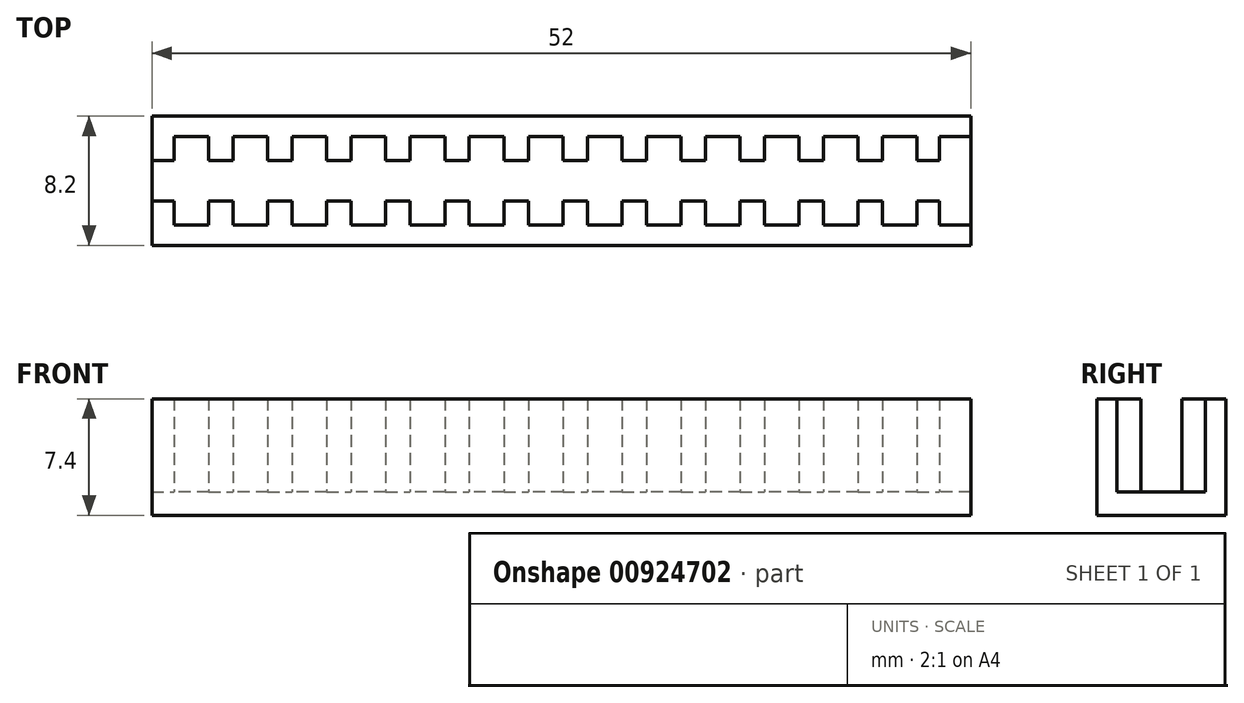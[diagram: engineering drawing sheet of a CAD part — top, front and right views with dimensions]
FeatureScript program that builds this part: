
annotation { "Feature Type Name" : "Feature", "Feature Type Description" : "" }
export const myFeature = defineFeature(function(context is Context, id is Id, definition is map)
    precondition{}
    {
        {
            assignVariable(context, id + "F0", {"name" : "Thickness", "anyValue" : 1.5});
        }
        {
            var Q0;
            Q0=qCreatedBy(makeId("Top.planeOp"),FACE);
            var sketch = newSketch(context, id + "F1", { "sketchPlane" : qUnion([Q0])});
            skLineSegment(sketch, "E0.bottom", {"start": v(0, 0) * mm, "end": v(52, 0) * mm});
            skLineSegment(sketch, "E0.top", {"start": v(0, -8.2) * mm, "end": v(52, -8.2) * mm});
            skLineSegment(sketch, "E0.left", {"start": v(0, 0) * mm, "end": v(0, -8.2) * mm});
            skLineSegment(sketch, "E0.right", {"start": v(52, 0) * mm, "end": v(52, -8.2) * mm});
            skLineSegment(sketch, "E1.top", {"start": v(0, -1.3) * mm, "end": v(52, -1.3) * mm});
            skLineSegment(sketch, "E1.left", {"start": v(0, 0) * mm, "end": v(0, -1.3) * mm});
            skLineSegment(sketch, "E1.right", {"start": v(52, 0) * mm, "end": v(52, -1.3) * mm});
            skLineSegment(sketch, "E2.bottom", {"start": v(0, -6.9) * mm, "end": v(52, -6.9) * mm});
            skLineSegment(sketch, "E2.left", {"start": v(0, -6.9) * mm, "end": v(0, -8.2) * mm});
            skLineSegment(sketch, "E2.right", {"start": v(52, -6.9) * mm, "end": v(52, -8.2) * mm});
            skLineSegment(sketch, "E3", {"start": v(2, -1.3) * mm, "end": v(2, 0) * mm, "construction": true});
            skLineSegment(sketch, "E4", {"start": v(2.26, -6.9) * mm, "end": v(2.26, -8.2) * mm, "construction": true});
            skSolve(sketch);
        }
        {
            var Q0;
            Q0 = qSketchRegion(id + "F1", true);
            extrude(context, id + "F2", {"entities" : qUnion([Q0]), "depth" : (getVariable(context, 'Thickness')) * mm, "offsetDistance" : 25 * mm});
        }
        {
            var Q0;
            Q0=makeQuery(id+"F1.imprint","IMPRINT",FACE,{"disambiguationData":[TD([[makeQuery(id+"F1.imprint","IMPRINT",EDGE,{"derivedFrom":sQuery(id+"F1.wireOp",EDGE,"E2.bottom")}),-1.0]])]});
            var Q1;
            Q1=makeQuery(id+"F1.imprint","IMPRINT",FACE,{"disambiguationData":[TD([[makeQuery(id+"F1.imprint","IMPRINT",EDGE,{"derivedFrom":sQuery(id+"F1.wireOp",EDGE,"E0.bottom")}),-1.0]])]});
            extrude(context, id + "F3", {"entities" : qUnion([Q0, Q1]), "operationType" : NewBodyOperationType.ADD, "depth" : (4.4 + getVariable(context, 'Thickness') * 2) * mm, "offsetDistance" : 25 * mm});
        }
        {
            var Q0;
            Q0=makeQuery(id+"F2.opExtrude","CAP_FACE",FACE,{"disambiguationData":[OSD([sQuery(id+"F1.wireOp",EDGE,"E0.left"),sQuery(id+"F1.wireOp",EDGE,"E0.right"),sQuery(id+"F1.wireOp",EDGE,"E0.bottom"),sQuery(id+"F1.wireOp",EDGE,"E1.left"),sQuery(id+"F1.wireOp",EDGE,"E1.right"),sQuery(id+"F1.wireOp",EDGE,"E0.top"),sQuery(id+"F1.wireOp",EDGE,"E2.left"),sQuery(id+"F1.wireOp",EDGE,"E2.right")])],"isStart":false});
            var sketch = newSketch(context, id + "F4", { "sketchPlane" : qUnion([Q0])});
            skLineSegment(sketch, "E5.bottom", {"start": v(0, -1.3) * mm, "end": v(1.4, -1.3) * mm});
            skLineSegment(sketch, "E5.top", {"start": v(0, -2.8) * mm, "end": v(1.4, -2.8) * mm});
            skLineSegment(sketch, "E5.left", {"start": v(0, -1.3) * mm, "end": v(0, -2.8) * mm});
            skLineSegment(sketch, "E5.right", {"start": v(1.4, -1.3) * mm, "end": v(1.4, -2.8) * mm});
            skLineSegment(sketch, "E6.bottom", {"start": v(0, -6.9) * mm, "end": v(1.4, -6.9) * mm});
            skLineSegment(sketch, "E6.top", {"start": v(0, -5.4) * mm, "end": v(1.4, -5.4) * mm});
            skLineSegment(sketch, "E6.left", {"start": v(0, -6.9) * mm, "end": v(0, -5.4) * mm});
            skLineSegment(sketch, "E6.right", {"start": v(1.4, -6.9) * mm, "end": v(1.4, -5.4) * mm});
            skLineSegment(sketch, "E7.bottom", {"start": v(3.6, -2.8) * mm, "end": v(5, -2.8) * mm});
            skLineSegment(sketch, "E7.top", {"start": v(3.6, -1.3) * mm, "end": v(5, -1.3) * mm});
            skLineSegment(sketch, "E7.left", {"start": v(3.6, -2.8) * mm, "end": v(3.6, -1.3) * mm});
            skLineSegment(sketch, "E7.right", {"start": v(5, -2.8) * mm, "end": v(5, -1.3) * mm});
            skLineSegment(sketch, "E8.bottom", {"start": v(3.6, -5.4) * mm, "end": v(5, -5.4) * mm});
            skLineSegment(sketch, "E8.top", {"start": v(3.6, -6.9) * mm, "end": v(5, -6.9) * mm});
            skLineSegment(sketch, "E8.left", {"start": v(3.6, -5.4) * mm, "end": v(3.6, -6.9) * mm});
            skLineSegment(sketch, "E8.right", {"start": v(5, -5.4) * mm, "end": v(5, -6.9) * mm});
            skLineSegment(sketch, "E9.1.0.0", {"start": v(3.75, -2.8) * mm, "end": v(5.15, -2.8) * mm});
            skLineSegment(sketch, "E9.1.0.1", {"start": v(5.15, -1.3) * mm, "end": v(5.15, -2.8) * mm});
            skLineSegment(sketch, "E9.1.0.2", {"start": v(3.75, -6.9) * mm, "end": v(5.15, -6.9) * mm});
            skLineSegment(sketch, "E9.1.0.3", {"start": v(3.75, -6.9) * mm, "end": v(3.75, -5.4) * mm});
            skLineSegment(sketch, "E9.1.0.4", {"start": v(7.35, -1.3) * mm, "end": v(8.75, -1.3) * mm});
            skLineSegment(sketch, "E9.1.0.5", {"start": v(3.75, -1.3) * mm, "end": v(5.15, -1.3) * mm});
            skLineSegment(sketch, "E9.1.0.6", {"start": v(7.35, -5.4) * mm, "end": v(8.75, -5.4) * mm});
            skLineSegment(sketch, "E9.1.0.7", {"start": v(7.35, -2.8) * mm, "end": v(7.35, -1.3) * mm});
            skLineSegment(sketch, "E9.1.0.8", {"start": v(5.15, -6.9) * mm, "end": v(5.15, -5.4) * mm});
            skLineSegment(sketch, "E9.1.0.9", {"start": v(7.35, -6.9) * mm, "end": v(8.75, -6.9) * mm});
            skLineSegment(sketch, "E9.1.0.10", {"start": v(8.75, -5.4) * mm, "end": v(8.75, -6.9) * mm});
            skLineSegment(sketch, "E9.1.0.11", {"start": v(3.75, -1.3) * mm, "end": v(3.75, -2.8) * mm});
            skLineSegment(sketch, "E9.1.0.12", {"start": v(7.35, -2.8) * mm, "end": v(8.75, -2.8) * mm});
            skLineSegment(sketch, "E9.1.0.13", {"start": v(7.35, -5.4) * mm, "end": v(7.35, -6.9) * mm});
            skLineSegment(sketch, "E9.1.0.14", {"start": v(3.75, -5.4) * mm, "end": v(5.15, -5.4) * mm});
            skLineSegment(sketch, "E9.1.0.15", {"start": v(8.75, -2.8) * mm, "end": v(8.75, -1.3) * mm});
            skLineSegment(sketch, "E9.2.0.0", {"start": v(7.5, -2.8) * mm, "end": v(8.9, -2.8) * mm});
            skLineSegment(sketch, "E9.2.0.1", {"start": v(8.9, -1.3) * mm, "end": v(8.9, -2.8) * mm});
            skLineSegment(sketch, "E9.2.0.2", {"start": v(7.5, -6.9) * mm, "end": v(8.9, -6.9) * mm});
            skLineSegment(sketch, "E9.2.0.3", {"start": v(7.5, -6.9) * mm, "end": v(7.5, -5.4) * mm});
            skLineSegment(sketch, "E9.2.0.4", {"start": v(11.1, -1.3) * mm, "end": v(12.5, -1.3) * mm});
            skLineSegment(sketch, "E9.2.0.5", {"start": v(7.5, -1.3) * mm, "end": v(8.9, -1.3) * mm});
            skLineSegment(sketch, "E9.2.0.6", {"start": v(11.1, -5.4) * mm, "end": v(12.5, -5.4) * mm});
            skLineSegment(sketch, "E9.2.0.7", {"start": v(11.1, -2.8) * mm, "end": v(11.1, -1.3) * mm});
            skLineSegment(sketch, "E9.2.0.8", {"start": v(8.9, -6.9) * mm, "end": v(8.9, -5.4) * mm});
            skLineSegment(sketch, "E9.2.0.9", {"start": v(11.1, -6.9) * mm, "end": v(12.5, -6.9) * mm});
            skLineSegment(sketch, "E9.2.0.10", {"start": v(12.5, -5.4) * mm, "end": v(12.5, -6.9) * mm});
            skLineSegment(sketch, "E9.2.0.11", {"start": v(7.5, -1.3) * mm, "end": v(7.5, -2.8) * mm});
            skLineSegment(sketch, "E9.2.0.12", {"start": v(11.1, -2.8) * mm, "end": v(12.5, -2.8) * mm});
            skLineSegment(sketch, "E9.2.0.13", {"start": v(11.1, -5.4) * mm, "end": v(11.1, -6.9) * mm});
            skLineSegment(sketch, "E9.2.0.14", {"start": v(7.5, -5.4) * mm, "end": v(8.9, -5.4) * mm});
            skLineSegment(sketch, "E9.2.0.15", {"start": v(12.5, -2.8) * mm, "end": v(12.5, -1.3) * mm});
            skLineSegment(sketch, "E9.direction1", {"start": v(0, -6.9) * mm, "end": v(3.75, -6.9) * mm, "construction": true});
            skLineSegment(sketch, "E10.0.3.0", {"start": v(11.25, -2.8) * mm, "end": v(12.65, -2.8) * mm});
            skLineSegment(sketch, "E10.3.3.0", {"start": v(12.65, -1.3) * mm, "end": v(12.65, -2.8) * mm});
            skLineSegment(sketch, "E10.6.3.0", {"start": v(11.25, -6.9) * mm, "end": v(12.65, -6.9) * mm});
            skLineSegment(sketch, "E10.9.3.0", {"start": v(11.25, -6.9) * mm, "end": v(11.25, -5.4) * mm});
            skLineSegment(sketch, "E10.12.3.0", {"start": v(14.85, -1.3) * mm, "end": v(16.25, -1.3) * mm});
            skLineSegment(sketch, "E10.15.3.0", {"start": v(11.25, -1.3) * mm, "end": v(12.65, -1.3) * mm});
            skLineSegment(sketch, "E10.18.3.0", {"start": v(14.85, -5.4) * mm, "end": v(16.25, -5.4) * mm});
            skLineSegment(sketch, "E10.21.3.0", {"start": v(14.85, -2.8) * mm, "end": v(14.85, -1.3) * mm});
            skLineSegment(sketch, "E10.24.3.0", {"start": v(12.65, -6.9) * mm, "end": v(12.65, -5.4) * mm});
            skLineSegment(sketch, "E10.27.3.0", {"start": v(14.85, -6.9) * mm, "end": v(16.25, -6.9) * mm});
            skLineSegment(sketch, "E10.30.3.0", {"start": v(16.25, -5.4) * mm, "end": v(16.25, -6.9) * mm});
            skLineSegment(sketch, "E10.33.3.0", {"start": v(11.25, -1.3) * mm, "end": v(11.25, -2.8) * mm});
            skLineSegment(sketch, "E10.36.3.0", {"start": v(14.85, -2.8) * mm, "end": v(16.25, -2.8) * mm});
            skLineSegment(sketch, "E10.39.3.0", {"start": v(14.85, -5.4) * mm, "end": v(14.85, -6.9) * mm});
            skLineSegment(sketch, "E10.42.3.0", {"start": v(11.25, -5.4) * mm, "end": v(12.65, -5.4) * mm});
            skLineSegment(sketch, "E10.45.3.0", {"start": v(16.25, -2.8) * mm, "end": v(16.25, -1.3) * mm});
            skLineSegment(sketch, "E10.0.4.0", {"start": v(15, -2.8) * mm, "end": v(16.4, -2.8) * mm});
            skLineSegment(sketch, "E10.3.4.0", {"start": v(16.4, -1.3) * mm, "end": v(16.4, -2.8) * mm});
            skLineSegment(sketch, "E10.6.4.0", {"start": v(15, -6.9) * mm, "end": v(16.4, -6.9) * mm});
            skLineSegment(sketch, "E10.9.4.0", {"start": v(15, -6.9) * mm, "end": v(15, -5.4) * mm});
            skLineSegment(sketch, "E10.12.4.0", {"start": v(18.6, -1.3) * mm, "end": v(20, -1.3) * mm});
            skLineSegment(sketch, "E10.15.4.0", {"start": v(15, -1.3) * mm, "end": v(16.4, -1.3) * mm});
            skLineSegment(sketch, "E10.18.4.0", {"start": v(18.6, -5.4) * mm, "end": v(20, -5.4) * mm});
            skLineSegment(sketch, "E10.21.4.0", {"start": v(18.6, -2.8) * mm, "end": v(18.6, -1.3) * mm});
            skLineSegment(sketch, "E10.24.4.0", {"start": v(16.4, -6.9) * mm, "end": v(16.4, -5.4) * mm});
            skLineSegment(sketch, "E10.27.4.0", {"start": v(18.6, -6.9) * mm, "end": v(20, -6.9) * mm});
            skLineSegment(sketch, "E10.30.4.0", {"start": v(20, -5.4) * mm, "end": v(20, -6.9) * mm});
            skLineSegment(sketch, "E10.33.4.0", {"start": v(15, -1.3) * mm, "end": v(15, -2.8) * mm});
            skLineSegment(sketch, "E10.36.4.0", {"start": v(18.6, -2.8) * mm, "end": v(20, -2.8) * mm});
            skLineSegment(sketch, "E10.39.4.0", {"start": v(18.6, -5.4) * mm, "end": v(18.6, -6.9) * mm});
            skLineSegment(sketch, "E10.42.4.0", {"start": v(15, -5.4) * mm, "end": v(16.4, -5.4) * mm});
            skLineSegment(sketch, "E10.45.4.0", {"start": v(20, -2.8) * mm, "end": v(20, -1.3) * mm});
            skLineSegment(sketch, "E10.0.5.0", {"start": v(18.75, -2.8) * mm, "end": v(20.15, -2.8) * mm});
            skLineSegment(sketch, "E10.3.5.0", {"start": v(20.15, -1.3) * mm, "end": v(20.15, -2.8) * mm});
            skLineSegment(sketch, "E10.6.5.0", {"start": v(18.75, -6.9) * mm, "end": v(20.15, -6.9) * mm});
            skLineSegment(sketch, "E10.9.5.0", {"start": v(18.75, -6.9) * mm, "end": v(18.75, -5.4) * mm});
            skLineSegment(sketch, "E10.12.5.0", {"start": v(22.35, -1.3) * mm, "end": v(23.75, -1.3) * mm});
            skLineSegment(sketch, "E10.15.5.0", {"start": v(18.75, -1.3) * mm, "end": v(20.15, -1.3) * mm});
            skLineSegment(sketch, "E10.18.5.0", {"start": v(22.35, -5.4) * mm, "end": v(23.75, -5.4) * mm});
            skLineSegment(sketch, "E10.21.5.0", {"start": v(22.35, -2.8) * mm, "end": v(22.35, -1.3) * mm});
            skLineSegment(sketch, "E10.24.5.0", {"start": v(20.15, -6.9) * mm, "end": v(20.15, -5.4) * mm});
            skLineSegment(sketch, "E10.27.5.0", {"start": v(22.35, -6.9) * mm, "end": v(23.75, -6.9) * mm});
            skLineSegment(sketch, "E10.30.5.0", {"start": v(23.75, -5.4) * mm, "end": v(23.75, -6.9) * mm});
            skLineSegment(sketch, "E10.33.5.0", {"start": v(18.75, -1.3) * mm, "end": v(18.75, -2.8) * mm});
            skLineSegment(sketch, "E10.36.5.0", {"start": v(22.35, -2.8) * mm, "end": v(23.75, -2.8) * mm});
            skLineSegment(sketch, "E10.39.5.0", {"start": v(22.35, -5.4) * mm, "end": v(22.35, -6.9) * mm});
            skLineSegment(sketch, "E10.42.5.0", {"start": v(18.75, -5.4) * mm, "end": v(20.15, -5.4) * mm});
            skLineSegment(sketch, "E10.45.5.0", {"start": v(23.75, -2.8) * mm, "end": v(23.75, -1.3) * mm});
            skLineSegment(sketch, "E10.0.6.0", {"start": v(22.5, -2.8) * mm, "end": v(23.9, -2.8) * mm});
            skLineSegment(sketch, "E10.3.6.0", {"start": v(23.9, -1.3) * mm, "end": v(23.9, -2.8) * mm});
            skLineSegment(sketch, "E10.6.6.0", {"start": v(22.5, -6.9) * mm, "end": v(23.9, -6.9) * mm});
            skLineSegment(sketch, "E10.9.6.0", {"start": v(22.5, -6.9) * mm, "end": v(22.5, -5.4) * mm});
            skLineSegment(sketch, "E10.12.6.0", {"start": v(26.1, -1.3) * mm, "end": v(27.5, -1.3) * mm});
            skLineSegment(sketch, "E10.15.6.0", {"start": v(22.5, -1.3) * mm, "end": v(23.9, -1.3) * mm});
            skLineSegment(sketch, "E10.18.6.0", {"start": v(26.1, -5.4) * mm, "end": v(27.5, -5.4) * mm});
            skLineSegment(sketch, "E10.21.6.0", {"start": v(26.1, -2.8) * mm, "end": v(26.1, -1.3) * mm});
            skLineSegment(sketch, "E10.24.6.0", {"start": v(23.9, -6.9) * mm, "end": v(23.9, -5.4) * mm});
            skLineSegment(sketch, "E10.27.6.0", {"start": v(26.1, -6.9) * mm, "end": v(27.5, -6.9) * mm});
            skLineSegment(sketch, "E10.30.6.0", {"start": v(27.5, -5.4) * mm, "end": v(27.5, -6.9) * mm});
            skLineSegment(sketch, "E10.33.6.0", {"start": v(22.5, -1.3) * mm, "end": v(22.5, -2.8) * mm});
            skLineSegment(sketch, "E10.36.6.0", {"start": v(26.1, -2.8) * mm, "end": v(27.5, -2.8) * mm});
            skLineSegment(sketch, "E10.39.6.0", {"start": v(26.1, -5.4) * mm, "end": v(26.1, -6.9) * mm});
            skLineSegment(sketch, "E10.42.6.0", {"start": v(22.5, -5.4) * mm, "end": v(23.9, -5.4) * mm});
            skLineSegment(sketch, "E10.45.6.0", {"start": v(27.5, -2.8) * mm, "end": v(27.5, -1.3) * mm});
            skLineSegment(sketch, "E10.0.7.0", {"start": v(26.25, -2.8) * mm, "end": v(27.65, -2.8) * mm});
            skLineSegment(sketch, "E10.3.7.0", {"start": v(27.65, -1.3) * mm, "end": v(27.65, -2.8) * mm});
            skLineSegment(sketch, "E10.6.7.0", {"start": v(26.25, -6.9) * mm, "end": v(27.65, -6.9) * mm});
            skLineSegment(sketch, "E10.9.7.0", {"start": v(26.25, -6.9) * mm, "end": v(26.25, -5.4) * mm});
            skLineSegment(sketch, "E10.12.7.0", {"start": v(29.85, -1.3) * mm, "end": v(31.25, -1.3) * mm});
            skLineSegment(sketch, "E10.15.7.0", {"start": v(26.25, -1.3) * mm, "end": v(27.65, -1.3) * mm});
            skLineSegment(sketch, "E10.18.7.0", {"start": v(29.85, -5.4) * mm, "end": v(31.25, -5.4) * mm});
            skLineSegment(sketch, "E10.21.7.0", {"start": v(29.85, -2.8) * mm, "end": v(29.85, -1.3) * mm});
            skLineSegment(sketch, "E10.24.7.0", {"start": v(27.65, -6.9) * mm, "end": v(27.65, -5.4) * mm});
            skLineSegment(sketch, "E10.27.7.0", {"start": v(29.85, -6.9) * mm, "end": v(31.25, -6.9) * mm});
            skLineSegment(sketch, "E10.30.7.0", {"start": v(31.25, -5.4) * mm, "end": v(31.25, -6.9) * mm});
            skLineSegment(sketch, "E10.33.7.0", {"start": v(26.25, -1.3) * mm, "end": v(26.25, -2.8) * mm});
            skLineSegment(sketch, "E10.36.7.0", {"start": v(29.85, -2.8) * mm, "end": v(31.25, -2.8) * mm});
            skLineSegment(sketch, "E10.39.7.0", {"start": v(29.85, -5.4) * mm, "end": v(29.85, -6.9) * mm});
            skLineSegment(sketch, "E10.42.7.0", {"start": v(26.25, -5.4) * mm, "end": v(27.65, -5.4) * mm});
            skLineSegment(sketch, "E10.45.7.0", {"start": v(31.25, -2.8) * mm, "end": v(31.25, -1.3) * mm});
            skLineSegment(sketch, "E11.0.8.0", {"start": v(30, -2.8) * mm, "end": v(31.4, -2.8) * mm});
            skLineSegment(sketch, "E11.3.8.0", {"start": v(31.4, -1.3) * mm, "end": v(31.4, -2.8) * mm});
            skLineSegment(sketch, "E11.6.8.0", {"start": v(30, -6.9) * mm, "end": v(31.4, -6.9) * mm});
            skLineSegment(sketch, "E11.9.8.0", {"start": v(30, -6.9) * mm, "end": v(30, -5.4) * mm});
            skLineSegment(sketch, "E11.12.8.0", {"start": v(33.6, -1.3) * mm, "end": v(35, -1.3) * mm});
            skLineSegment(sketch, "E11.15.8.0", {"start": v(30, -1.3) * mm, "end": v(31.4, -1.3) * mm});
            skLineSegment(sketch, "E11.18.8.0", {"start": v(33.6, -5.4) * mm, "end": v(35, -5.4) * mm});
            skLineSegment(sketch, "E11.21.8.0", {"start": v(33.6, -2.8) * mm, "end": v(33.6, -1.3) * mm});
            skLineSegment(sketch, "E11.24.8.0", {"start": v(31.4, -6.9) * mm, "end": v(31.4, -5.4) * mm});
            skLineSegment(sketch, "E11.27.8.0", {"start": v(33.6, -6.9) * mm, "end": v(35, -6.9) * mm});
            skLineSegment(sketch, "E11.30.8.0", {"start": v(35, -5.4) * mm, "end": v(35, -6.9) * mm});
            skLineSegment(sketch, "E11.33.8.0", {"start": v(30, -1.3) * mm, "end": v(30, -2.8) * mm});
            skLineSegment(sketch, "E11.36.8.0", {"start": v(33.6, -2.8) * mm, "end": v(35, -2.8) * mm});
            skLineSegment(sketch, "E11.39.8.0", {"start": v(33.6, -5.4) * mm, "end": v(33.6, -6.9) * mm});
            skLineSegment(sketch, "E11.42.8.0", {"start": v(30, -5.4) * mm, "end": v(31.4, -5.4) * mm});
            skLineSegment(sketch, "E11.45.8.0", {"start": v(35, -2.8) * mm, "end": v(35, -1.3) * mm});
            skLineSegment(sketch, "E12.0.9.0", {"start": v(33.75, -2.8) * mm, "end": v(35.15, -2.8) * mm});
            skLineSegment(sketch, "E12.3.9.0", {"start": v(35.15, -1.3) * mm, "end": v(35.15, -2.8) * mm});
            skLineSegment(sketch, "E12.6.9.0", {"start": v(33.75, -6.9) * mm, "end": v(35.15, -6.9) * mm});
            skLineSegment(sketch, "E12.9.9.0", {"start": v(33.75, -6.9) * mm, "end": v(33.75, -5.4) * mm});
            skLineSegment(sketch, "E12.12.9.0", {"start": v(37.35, -1.3) * mm, "end": v(38.75, -1.3) * mm});
            skLineSegment(sketch, "E12.15.9.0", {"start": v(33.75, -1.3) * mm, "end": v(35.15, -1.3) * mm});
            skLineSegment(sketch, "E12.18.9.0", {"start": v(37.35, -5.4) * mm, "end": v(38.75, -5.4) * mm});
            skLineSegment(sketch, "E12.21.9.0", {"start": v(37.35, -2.8) * mm, "end": v(37.35, -1.3) * mm});
            skLineSegment(sketch, "E12.24.9.0", {"start": v(35.15, -6.9) * mm, "end": v(35.15, -5.4) * mm});
            skLineSegment(sketch, "E12.27.9.0", {"start": v(37.35, -6.9) * mm, "end": v(38.75, -6.9) * mm});
            skLineSegment(sketch, "E12.30.9.0", {"start": v(38.75, -5.4) * mm, "end": v(38.75, -6.9) * mm});
            skLineSegment(sketch, "E12.33.9.0", {"start": v(33.75, -1.3) * mm, "end": v(33.75, -2.8) * mm});
            skLineSegment(sketch, "E12.36.9.0", {"start": v(37.35, -2.8) * mm, "end": v(38.75, -2.8) * mm});
            skLineSegment(sketch, "E12.39.9.0", {"start": v(37.35, -5.4) * mm, "end": v(37.35, -6.9) * mm});
            skLineSegment(sketch, "E12.42.9.0", {"start": v(33.75, -5.4) * mm, "end": v(35.15, -5.4) * mm});
            skLineSegment(sketch, "E12.45.9.0", {"start": v(38.75, -2.8) * mm, "end": v(38.75, -1.3) * mm});
            skLineSegment(sketch, "E13.0.10.0", {"start": v(37.5, -2.8) * mm, "end": v(38.9, -2.8) * mm});
            skLineSegment(sketch, "E13.3.10.0", {"start": v(38.9, -1.3) * mm, "end": v(38.9, -2.8) * mm});
            skLineSegment(sketch, "E13.6.10.0", {"start": v(37.5, -6.9) * mm, "end": v(38.9, -6.9) * mm});
            skLineSegment(sketch, "E13.9.10.0", {"start": v(37.5, -6.9) * mm, "end": v(37.5, -5.4) * mm});
            skLineSegment(sketch, "E13.12.10.0", {"start": v(41.1, -1.3) * mm, "end": v(42.5, -1.3) * mm});
            skLineSegment(sketch, "E13.15.10.0", {"start": v(37.5, -1.3) * mm, "end": v(38.9, -1.3) * mm});
            skLineSegment(sketch, "E13.18.10.0", {"start": v(41.1, -5.4) * mm, "end": v(42.5, -5.4) * mm});
            skLineSegment(sketch, "E13.21.10.0", {"start": v(41.1, -2.8) * mm, "end": v(41.1, -1.3) * mm});
            skLineSegment(sketch, "E13.24.10.0", {"start": v(38.9, -6.9) * mm, "end": v(38.9, -5.4) * mm});
            skLineSegment(sketch, "E13.27.10.0", {"start": v(41.1, -6.9) * mm, "end": v(42.5, -6.9) * mm});
            skLineSegment(sketch, "E13.30.10.0", {"start": v(42.5, -5.4) * mm, "end": v(42.5, -6.9) * mm});
            skLineSegment(sketch, "E13.33.10.0", {"start": v(37.5, -1.3) * mm, "end": v(37.5, -2.8) * mm});
            skLineSegment(sketch, "E13.36.10.0", {"start": v(41.1, -2.8) * mm, "end": v(42.5, -2.8) * mm});
            skLineSegment(sketch, "E13.39.10.0", {"start": v(41.1, -5.4) * mm, "end": v(41.1, -6.9) * mm});
            skLineSegment(sketch, "E13.42.10.0", {"start": v(37.5, -5.4) * mm, "end": v(38.9, -5.4) * mm});
            skLineSegment(sketch, "E13.45.10.0", {"start": v(42.5, -2.8) * mm, "end": v(42.5, -1.3) * mm});
            skLineSegment(sketch, "E13.0.11.0", {"start": v(41.25, -2.8) * mm, "end": v(42.65, -2.8) * mm});
            skLineSegment(sketch, "E13.3.11.0", {"start": v(42.65, -1.3) * mm, "end": v(42.65, -2.8) * mm});
            skLineSegment(sketch, "E13.6.11.0", {"start": v(41.25, -6.9) * mm, "end": v(42.65, -6.9) * mm});
            skLineSegment(sketch, "E13.9.11.0", {"start": v(41.25, -6.9) * mm, "end": v(41.25, -5.4) * mm});
            skLineSegment(sketch, "E13.12.11.0", {"start": v(44.85, -1.3) * mm, "end": v(46.25, -1.3) * mm});
            skLineSegment(sketch, "E13.15.11.0", {"start": v(41.25, -1.3) * mm, "end": v(42.65, -1.3) * mm});
            skLineSegment(sketch, "E13.18.11.0", {"start": v(44.85, -5.4) * mm, "end": v(46.25, -5.4) * mm});
            skLineSegment(sketch, "E13.21.11.0", {"start": v(44.85, -2.8) * mm, "end": v(44.85, -1.3) * mm});
            skLineSegment(sketch, "E13.24.11.0", {"start": v(42.65, -6.9) * mm, "end": v(42.65, -5.4) * mm});
            skLineSegment(sketch, "E13.27.11.0", {"start": v(44.85, -6.9) * mm, "end": v(46.25, -6.9) * mm});
            skLineSegment(sketch, "E13.30.11.0", {"start": v(46.25, -5.4) * mm, "end": v(46.25, -6.9) * mm});
            skLineSegment(sketch, "E13.33.11.0", {"start": v(41.25, -1.3) * mm, "end": v(41.25, -2.8) * mm});
            skLineSegment(sketch, "E13.36.11.0", {"start": v(44.85, -2.8) * mm, "end": v(46.25, -2.8) * mm});
            skLineSegment(sketch, "E13.39.11.0", {"start": v(44.85, -5.4) * mm, "end": v(44.85, -6.9) * mm});
            skLineSegment(sketch, "E13.42.11.0", {"start": v(41.25, -5.4) * mm, "end": v(42.65, -5.4) * mm});
            skLineSegment(sketch, "E13.45.11.0", {"start": v(46.25, -2.8) * mm, "end": v(46.25, -1.3) * mm});
            skLineSegment(sketch, "E14.0.12.0", {"start": v(45, -2.8) * mm, "end": v(46.4, -2.8) * mm});
            skLineSegment(sketch, "E14.3.12.0", {"start": v(46.4, -1.3) * mm, "end": v(46.4, -2.8) * mm});
            skLineSegment(sketch, "E14.6.12.0", {"start": v(45, -6.9) * mm, "end": v(46.4, -6.9) * mm});
            skLineSegment(sketch, "E14.9.12.0", {"start": v(45, -6.9) * mm, "end": v(45, -5.4) * mm});
            skLineSegment(sketch, "E14.12.12.0", {"start": v(48.6, -1.3) * mm, "end": v(50, -1.3) * mm});
            skLineSegment(sketch, "E14.15.12.0", {"start": v(45, -1.3) * mm, "end": v(46.4, -1.3) * mm});
            skLineSegment(sketch, "E14.18.12.0", {"start": v(48.6, -5.4) * mm, "end": v(50, -5.4) * mm});
            skLineSegment(sketch, "E14.21.12.0", {"start": v(48.6, -2.8) * mm, "end": v(48.6, -1.3) * mm});
            skLineSegment(sketch, "E14.24.12.0", {"start": v(46.4, -6.9) * mm, "end": v(46.4, -5.4) * mm});
            skLineSegment(sketch, "E14.27.12.0", {"start": v(48.6, -6.9) * mm, "end": v(50, -6.9) * mm});
            skLineSegment(sketch, "E14.30.12.0", {"start": v(50, -5.4) * mm, "end": v(50, -6.9) * mm});
            skLineSegment(sketch, "E14.33.12.0", {"start": v(45, -1.3) * mm, "end": v(45, -2.8) * mm});
            skLineSegment(sketch, "E14.36.12.0", {"start": v(48.6, -2.8) * mm, "end": v(50, -2.8) * mm});
            skLineSegment(sketch, "E14.39.12.0", {"start": v(48.6, -5.4) * mm, "end": v(48.6, -6.9) * mm});
            skLineSegment(sketch, "E14.42.12.0", {"start": v(45, -5.4) * mm, "end": v(46.4, -5.4) * mm});
            skLineSegment(sketch, "E14.45.12.0", {"start": v(50, -2.8) * mm, "end": v(50, -1.3) * mm});
            skSolve(sketch);
        }
        {
            var Q0;
            Q0 = qSketchRegion(id + "F4", true);
            extrude(context, id + "F5", {"entities" : qUnion([Q0]), "operationType" : NewBodyOperationType.ADD, "depth" : (4.4 + getVariable(context, 'Thickness')) * mm, "offsetDistance" : 25 * mm});
        }
    });
